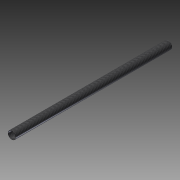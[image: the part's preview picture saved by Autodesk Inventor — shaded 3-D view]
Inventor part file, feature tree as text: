
AUTODESK INVENTOR PART (.ipt)
format: ipt  version: 2015 (Build 190159000, 159)  size: 88,064 bytes
history: native  units: in
note: dims shown in document units (in); Inventor stores cm internally (conversion verified against a paired STEP export)
features: extrude x1, sketch x1
ambient origin geometry x8: Origin, YZ Plane, XZ Plane, XY Plane, X Axis, Y Axis, Z Axis, Center Point
bodies: Solid1 (feature_tree)
feature tree (2):
  extrude  "Extrusion1"  Depth=0.4528in
  sketch  "Sketch1"  dims[d0=0.4921in d1=0.4528in d2=19.685in d3=0.0in]
